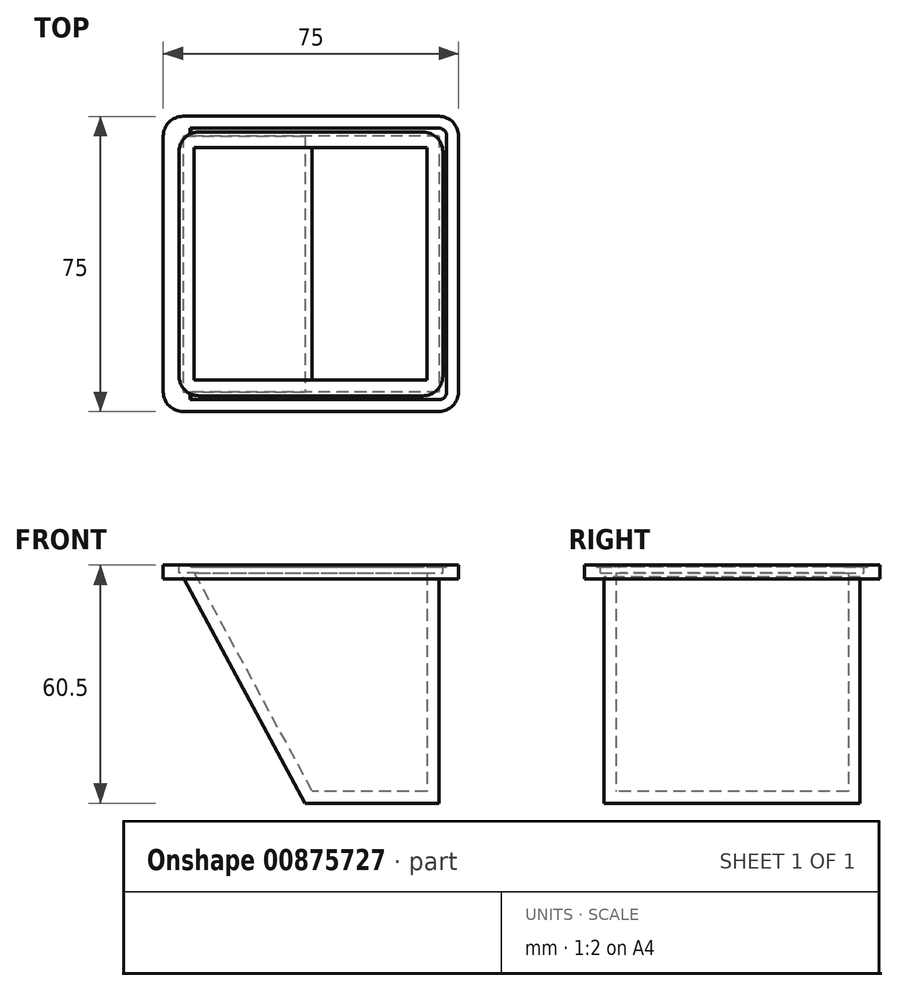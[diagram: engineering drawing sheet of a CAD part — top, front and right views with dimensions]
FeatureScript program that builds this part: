
annotation { "Feature Type Name" : "Feature", "Feature Type Description" : "" }
export const myFeature = defineFeature(function(context is Context, id is Id, definition is map)
    precondition{}
    {
        {
            var Q0;
            Q0=qCreatedBy(makeId("Top.planeOp"),FACE);
            var sketch = newSketch(context, id + "F0", { "sketchPlane" : qUnion([Q0])});
            skLineSegment(sketch, "E0.bottom", {"start": v(-36.02, 36.3) * mm, "end": v(38.98, 36.3) * mm});
            skLineSegment(sketch, "E0.top", {"start": v(-36.02, -38.7) * mm, "end": v(38.98, -38.7) * mm});
            skLineSegment(sketch, "E0.left", {"start": v(-36.02, 36.3) * mm, "end": v(-36.02, -38.7) * mm});
            skLineSegment(sketch, "E0.right", {"start": v(38.98, 36.3) * mm, "end": v(38.98, -38.7) * mm});
            skSolve(sketch);
        }
        {
            var Q0;
            Q0=makeQuery(id+"F0.imprint","IMPRINT",FACE,{"disambiguationData":[TD([[makeQuery(id+"F0.imprint","IMPRINT",EDGE,{"derivedFrom":sQuery(id+"F0.wireOp",EDGE,"E0.bottom")}),-1.0]])]});
            extrude(context, id + "F1", {"entities" : qUnion([Q0]), "depth" : 3.5 * mm, "offsetDistance" : 25 * mm});
        }
        {
            var Q0;
            Q0=makeQuery(id+"F1.opExtrude","CAP_FACE",FACE,{"disambiguationData":[OSD([sQuery(id+"F0.wireOp",EDGE,"E0.bottom"),sQuery(id+"F0.wireOp",EDGE,"E0.top"),sQuery(id+"F0.wireOp",EDGE,"E0.left"),sQuery(id+"F0.wireOp",EDGE,"E0.right")])],"isStart":false});
            var sketch = newSketch(context, id + "F2", { "sketchPlane" : qUnion([Q0])});
            skLineSegment(sketch, "E1.bottom", {"start": v(-31.02, 31.3) * mm, "end": v(33.98, 31.3) * mm});
            skLineSegment(sketch, "E1.top", {"start": v(-31.02, -33.7) * mm, "end": v(33.98, -33.7) * mm});
            skLineSegment(sketch, "E1.left", {"start": v(-31.02, 31.3) * mm, "end": v(-31.02, -33.7) * mm});
            skLineSegment(sketch, "E1.right", {"start": v(33.98, 31.3) * mm, "end": v(33.98, -33.7) * mm});
            skSolve(sketch);
        }
        {
            var Q0;
            Q0 = qSketchRegion(id + "F2", true);
            extrude(context, id + "F3", {"entities" : qUnion([Q0]), "operationType" : NewBodyOperationType.REMOVE, "oppositeDirection" : true, "depth" : 3.5 * mm, "offsetDistance" : 25 * mm});
        }
        {
            var Q0;
            Q0=makeQuery(id+"F1.opExtrude","SWEPT_EDGE",EDGE,{"disambiguationData":[OSD([sQuery(id+"F0.wireOp",EDGE,"E0.top"),sQuery(id+"F0.wireOp",EDGE,"E0.right")])]});
            var Q1;
            Q1=makeQuery(id+"F1.opExtrude","SWEPT_EDGE",EDGE,{"disambiguationData":[OSD([sQuery(id+"F0.wireOp",EDGE,"E0.top"),sQuery(id+"F0.wireOp",EDGE,"E0.left")])]});
            var Q2;
            Q2=makeQuery(id+"F1.opExtrude","SWEPT_EDGE",EDGE,{"disambiguationData":[OSD([sQuery(id+"F0.wireOp",EDGE,"E0.bottom"),sQuery(id+"F0.wireOp",EDGE,"E0.right")])]});
            var Q3;
            Q3=makeQuery(id+"F1.opExtrude","SWEPT_EDGE",EDGE,{"disambiguationData":[OSD([sQuery(id+"F0.wireOp",EDGE,"E0.bottom"),sQuery(id+"F0.wireOp",EDGE,"E0.left")])]});
            fillet(context, id + "F4", {"entities" : qUnion([Q0, Q1, Q2, Q3]), "radius" : 5 * mm, "tangentPropagation" : true, "allowEdgeOverflow" : false});
        }
        {
            var Q0;
            Q0=makeQuery(id+"F3.boolean.opBoolean","COPY",FACE,{"derivedFrom":makeQuery(id+"F3.opExtrude","SWEPT_FACE",FACE,{"disambiguationData":[OSD([sQuery(id+"F2.wireOp",EDGE,"E1.top")])]})});
            var sketch = newSketch(context, id + "F5", { "sketchPlane" : qUnion([Q0])});
            skLineSegment(sketch, "E2.bottom", {"start": v(-33.98, 3.5) * mm, "end": v(31.02, 3.5) * mm});
            skLineSegment(sketch, "E2.top", {"start": v(-33.98, -57) * mm, "end": v(0, -57) * mm});
            skLineSegment(sketch, "E2.left", {"start": v(-33.98, 3.5) * mm, "end": v(-33.98, -57) * mm});
            skLineSegment(sketch, "E2.right", {"start": v(31.02, 3.5) * mm, "end": v(31.02, 0.5) * mm});
            skLineSegment(sketch, "E3", {"start": v(31.02, 0.5) * mm, "end": v(0, -57) * mm});
            skPoint(sketch, "E4.orphan", {"position": v(31.02, -57) * mm});
            skSolve(sketch);
        }
        {
            var Q0;
            Q0 = qSketchRegion(id + "F5", true);
            extrude(context, id + "F6", {"entities" : qUnion([Q0]), "operationType" : NewBodyOperationType.ADD, "depth" : 65 * mm, "offsetDistance" : 25 * mm});
        }
        {
            var Q0;
            Q0=makeQuery(id+"F6.boolean.opBoolean","MERGE",FACE,{"derivedFrom":[makeQuery(id+"F1.opExtrude","CAP_FACE",FACE,{"disambiguationData":[OSD([sQuery(id+"F0.wireOp",EDGE,"E0.bottom"),sQuery(id+"F0.wireOp",EDGE,"E0.top"),sQuery(id+"F0.wireOp",EDGE,"E0.left"),sQuery(id+"F0.wireOp",EDGE,"E0.right")])],"isStart":false}),makeQuery(id+"F6.opExtrude","SWEPT_FACE",FACE,{"disambiguationData":[OSD([sQuery(id+"F5.wireOp",EDGE,"E2.bottom")])]})]});
            shell(context, id + "F7", {"entities" : qUnion([Q0]), "thickness" : 3 * mm});
        }
        {
            var Q0;
            Q0=makeQuery(id+"F2.imprint","IMPRINT",FACE,{"disambiguationData":[TD([[makeQuery(id+"F2.imprint","IMPRINT",EDGE,{"derivedFrom":sQuery(id+"F2.wireOp",EDGE,"E1.bottom")}),1.0]])]});
            var sketch = newSketch(context, id + "F8", { "sketchPlane" : qUnion([Q0])});
            skLineSegment(sketch, "E5.bottom", {"start": v(-32.02, 32.3) * mm, "end": v(34.98, 32.3) * mm});
            skLineSegment(sketch, "E5.top", {"start": v(-32.02, -34.7) * mm, "end": v(34.98, -34.7) * mm});
            skLineSegment(sketch, "E5.left", {"start": v(-32.02, 32.3) * mm, "end": v(-32.02, -34.7) * mm});
            skLineSegment(sketch, "E5.right", {"start": v(34.98, 32.3) * mm, "end": v(34.98, -34.7) * mm});
            skSolve(sketch);
        }
        {
            var Q0;
            Q0 = qSketchRegion(id + "F8", true);
            extrude(context, id + "F9", {"entities" : qUnion([Q0]), "operationType" : NewBodyOperationType.REMOVE, "oppositeDirection" : true, "depth" : 2 * mm, "offsetDistance" : 25 * mm});
        }
        {
            var Q0;
            Q0=makeQuery(id+"F9.boolean.opBoolean","COPY",EDGE,{"derivedFrom":makeQuery(id+"F9.opExtrude","SWEPT_EDGE",EDGE,{"disambiguationData":[OSD([sQuery(id+"F8.wireOp",EDGE,"E5.bottom"),sQuery(id+"F8.wireOp",EDGE,"E5.left")])]})});
            var Q1;
            Q1=makeQuery(id+"F9.boolean.opBoolean","COPY",EDGE,{"derivedFrom":makeQuery(id+"F9.opExtrude","SWEPT_EDGE",EDGE,{"disambiguationData":[OSD([sQuery(id+"F8.wireOp",EDGE,"E5.bottom"),sQuery(id+"F8.wireOp",EDGE,"E5.right")])]})});
            var Q2;
            Q2=makeQuery(id+"F9.boolean.opBoolean","COPY",EDGE,{"derivedFrom":makeQuery(id+"F9.opExtrude","SWEPT_EDGE",EDGE,{"disambiguationData":[OSD([sQuery(id+"F8.wireOp",EDGE,"E5.top"),sQuery(id+"F8.wireOp",EDGE,"E5.left")])]})});
            var Q3;
            Q3=makeQuery(id+"F9.boolean.opBoolean","COPY",EDGE,{"derivedFrom":makeQuery(id+"F9.opExtrude","SWEPT_EDGE",EDGE,{"disambiguationData":[OSD([sQuery(id+"F8.wireOp",EDGE,"E5.top"),sQuery(id+"F8.wireOp",EDGE,"E5.right")])]})});
            fillet(context, id + "F10", {"entities" : qUnion([Q0, Q1, Q2, Q3]), "radius" : 5 * mm, "tangentPropagation" : true, "allowEdgeOverflow" : false});
        }
    });
